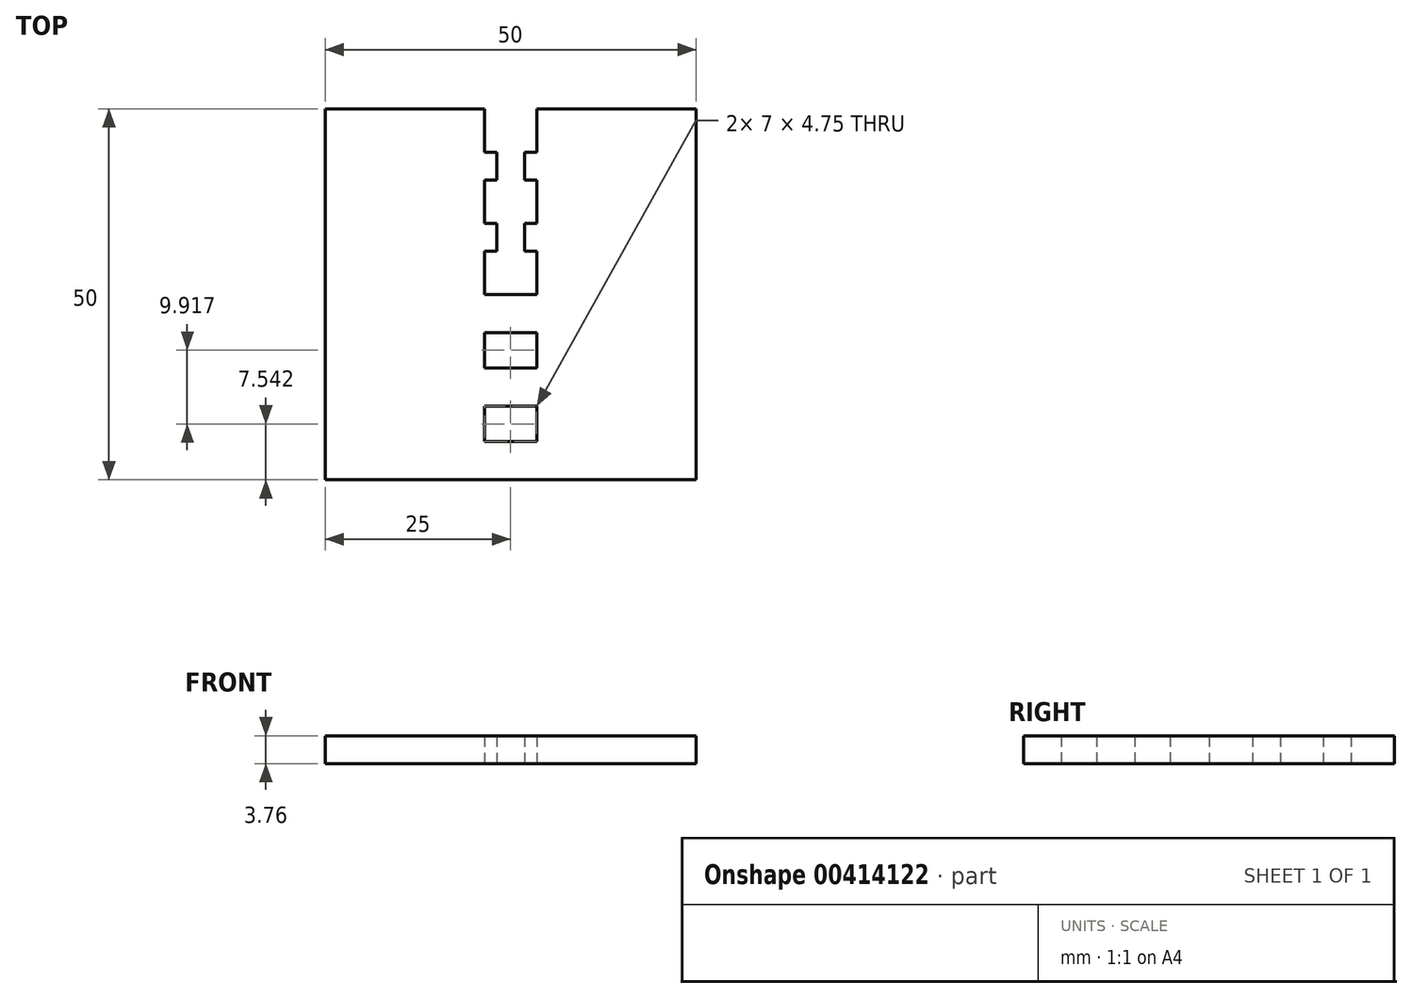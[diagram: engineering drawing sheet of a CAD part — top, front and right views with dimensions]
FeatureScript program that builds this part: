
annotation { "Feature Type Name" : "Feature", "Feature Type Description" : "" }
export const myFeature = defineFeature(function(context is Context, id is Id, definition is map)
    precondition{}
    {
        {
            assignVariable(context, id + "F0", {"name" : "material_thickness", "anyValue" : 3.75});
        }
        {
            var Q0;
            Q0=qCreatedBy(makeId("Top.planeOp"),FACE);
            var sketch = newSketch(context, id + "F1", { "sketchPlane" : qUnion([Q0])});
            skLineSegment(sketch, "E0.bottom", {"start": v(25, -25) * mm, "end": v(-25, -25) * mm});
            skLineSegment(sketch, "E0.top", {"start": v(25, 25) * mm, "end": v(3.5, 25) * mm});
            skLineSegment(sketch, "E0.left", {"start": v(25, -25) * mm, "end": v(25, 25) * mm});
            skLineSegment(sketch, "E0.right", {"start": v(-25, -25) * mm, "end": v(-25, 25) * mm});
            skPoint(sketch, "E0.middle", {"position": v(0, 0) * mm});
            skLineSegment(sketch, "E1", {"start": v(-3.5, 25) * mm, "end": v(-3.5, 19.17) * mm});
            skLineSegment(sketch, "E2", {"start": v(-3.5, 0) * mm, "end": v(3.5, 0) * mm});
            skLineSegment(sketch, "E3", {"start": v(3.5, 0) * mm, "end": v(3.5, 25) * mm});
            skLineSegment(sketch, "E4.trimOffspring", {"start": v(-3.5, 25) * mm, "end": v(-25, 25) * mm});
            skLineSegment(sketch, "E5", {"start": v(-3.5, 5.83) * mm, "end": v(-1.88, 5.83) * mm});
            skLineSegment(sketch, "E6", {"start": v(-1.88, 5.83) * mm, "end": v(-1.88, 9.58) * mm});
            skLineSegment(sketch, "E7", {"start": v(-1.88, 9.58) * mm, "end": v(-3.5, 9.58) * mm});
            skLineSegment(sketch, "E8.trimOffspring", {"start": v(-3.5, 5.83) * mm, "end": v(-3.5, 0) * mm});
            skLineSegment(sketch, "E9", {"start": v(-3.5, 15.42) * mm, "end": v(-1.88, 15.42) * mm});
            skLineSegment(sketch, "E10", {"start": v(-1.88, 15.42) * mm, "end": v(-1.88, 19.17) * mm});
            skLineSegment(sketch, "E11", {"start": v(-1.88, 19.17) * mm, "end": v(-3.5, 19.17) * mm});
            skLineSegment(sketch, "E12.trimOffspring", {"start": v(-3.5, 15.42) * mm, "end": v(-3.5, 9.58) * mm});
            skLineSegment(sketch, "E13", {"start": v(0, 0) * mm, "end": v(0, 25) * mm, "construction": true});
            skLineSegment(sketch, "E14", {"start": v(0, 0) * mm, "end": v(0, -25) * mm});
            skSolve(sketch);
        }
        {
            var Q0;
            {var subQ1=sQuery(id+"F1.wireOp",EDGE,"E0.right");Q0=makeQuery(id+"F1.imprint","IMPRINT",FACE,{"disambiguationData":[TD([[makeQuery(id+"F1.imprint","IMPRINT",EDGE,{"derivedFrom":subQ1}),-1.0]])]});}
            extrude(context, id + "F2", {"entities" : qUnion([Q0]), "endBound" : BoundingType.SYMMETRIC, "depth" : (getVariable(context, 'material_thickness')) * mm});
        }
        {
            var Q0;
            Q0=makeQuery(id+"F2.opExtrude","SWEPT_BODY",BODY,{"disambiguationData":[OSD([sQuery(id+"F1.wireOp",EDGE,"E0.bottom"),sQuery(id+"F1.wireOp",EDGE,"E0.right"),sQuery(id+"F1.wireOp",EDGE,"E1"),sQuery(id+"F1.wireOp",EDGE,"E2"),sQuery(id+"F1.wireOp",EDGE,"E4.trimOffspring"),sQuery(id+"F1.wireOp",EDGE,"E5"),sQuery(id+"F1.wireOp",EDGE,"E6"),sQuery(id+"F1.wireOp",EDGE,"E7"),sQuery(id+"F1.wireOp",EDGE,"E8.trimOffspring"),sQuery(id+"F1.wireOp",EDGE,"E9"),sQuery(id+"F1.wireOp",EDGE,"E10"),sQuery(id+"F1.wireOp",EDGE,"E11"),sQuery(id+"F1.wireOp",EDGE,"E12.trimOffspring"),sQuery(id+"F1.wireOp",EDGE,"E14")])]});
            var Q1;
            Q1=makeQuery(id+"F2.opExtrude","SWEPT_FACE",FACE,{"disambiguationData":[OSD([sQuery(id+"F1.wireOp",EDGE,"E14")])]});
            mirror(context, id + "F3", {"operationType" : NewBodyOperationType.ADD, "entities" : qUnion([Q0]), "mirrorPlane" : qUnion([Q1])});
        }
        {
            var Q0;
            {var subQ0=makeQuery(id+"F2.opExtrude","CAP_FACE",FACE,{"disambiguationData":[OSD([sQuery(id+"F1.wireOp",EDGE,"E0.bottom"),sQuery(id+"F1.wireOp",EDGE,"E0.right"),sQuery(id+"F1.wireOp",EDGE,"E1"),sQuery(id+"F1.wireOp",EDGE,"E2"),sQuery(id+"F1.wireOp",EDGE,"E4.trimOffspring"),sQuery(id+"F1.wireOp",EDGE,"E5"),sQuery(id+"F1.wireOp",EDGE,"E6"),sQuery(id+"F1.wireOp",EDGE,"E7"),sQuery(id+"F1.wireOp",EDGE,"E8.trimOffspring"),sQuery(id+"F1.wireOp",EDGE,"E9"),sQuery(id+"F1.wireOp",EDGE,"E10"),sQuery(id+"F1.wireOp",EDGE,"E11"),sQuery(id+"F1.wireOp",EDGE,"E12.trimOffspring"),sQuery(id+"F1.wireOp",EDGE,"E14")])],"isStart":false});Q0=makeQuery(id+"F3.boolean.opBoolean","MERGE",FACE,{"derivedFrom":[subQ0,makeQuery(id+"F3.opPattern","COPY",FACE,{"derivedFrom":subQ0,"instanceName":"1"})]});}
            var sketch = newSketch(context, id + "F4", { "sketchPlane" : qUnion([Q0])});
            skLineSegment(sketch, "E15", {"start": v(0, 0) * mm, "end": v(0, -25) * mm, "construction": true});
            skLineSegment(sketch, "E16.bottom", {"start": v(3.5, -5.17) * mm, "end": v(-3.5, -5.17) * mm});
            skLineSegment(sketch, "E16.top", {"start": v(3.5, -9.92) * mm, "end": v(-3.5, -9.92) * mm});
            skLineSegment(sketch, "E16.left", {"start": v(3.5, -5.17) * mm, "end": v(3.5, -9.92) * mm});
            skLineSegment(sketch, "E16.right", {"start": v(-3.5, -5.17) * mm, "end": v(-3.5, -9.92) * mm});
            skPoint(sketch, "E16.middle", {"position": v(0, -7.54) * mm});
            skLineSegment(sketch, "E17.bottom", {"start": v(3.5, -15.08) * mm, "end": v(-3.5, -15.08) * mm});
            skLineSegment(sketch, "E17.top", {"start": v(3.5, -19.83) * mm, "end": v(-3.5, -19.83) * mm});
            skLineSegment(sketch, "E17.left", {"start": v(3.5, -15.08) * mm, "end": v(3.5, -19.83) * mm});
            skLineSegment(sketch, "E17.right", {"start": v(-3.5, -15.08) * mm, "end": v(-3.5, -19.83) * mm});
            skPoint(sketch, "E17.middle", {"position": v(0, -17.46) * mm});
            skLineSegment(sketch, "E18", {"start": v(-3.5, -5.17) * mm, "end": v(-3.5, 0) * mm, "construction": true});
            skLineSegment(sketch, "E19", {"start": v(-3.5, -9.92) * mm, "end": v(-3.5, -15.08) * mm, "construction": true});
            skLineSegment(sketch, "E20.0", {"start": v(-1.88, 5.83) * mm, "end": v(-1.88, 9.58) * mm, "construction": true});
            skLineSegment(sketch, "E21.0", {"start": v(-3.5, 15.42) * mm, "end": v(-3.5, 9.58) * mm, "construction": true});
            skLineSegment(sketch, "E22", {"start": v(-3.5, -19.83) * mm, "end": v(-3.5, -25) * mm, "construction": true});
            skSolve(sketch);
        }
        {
            var Q0;
            Q0=makeQuery(id+"F4.imprint","IMPRINT",FACE,{"disambiguationData":[TD([[makeQuery(id+"F4.imprint","IMPRINT",EDGE,{"derivedFrom":sQuery(id+"F4.wireOp",EDGE,"E16.bottom")}),1.0]])]});
            var Q1;
            Q1=makeQuery(id+"F4.imprint","IMPRINT",FACE,{"disambiguationData":[TD([[makeQuery(id+"F4.imprint","IMPRINT",EDGE,{"derivedFrom":sQuery(id+"F4.wireOp",EDGE,"E17.bottom")}),1.0]])]});
            extrude(context, id + "F5", {"entities" : qUnion([Q0, Q1]), "operationType" : NewBodyOperationType.REMOVE, "oppositeDirection" : true, "depth" : 25 * mm});
        }
    });
